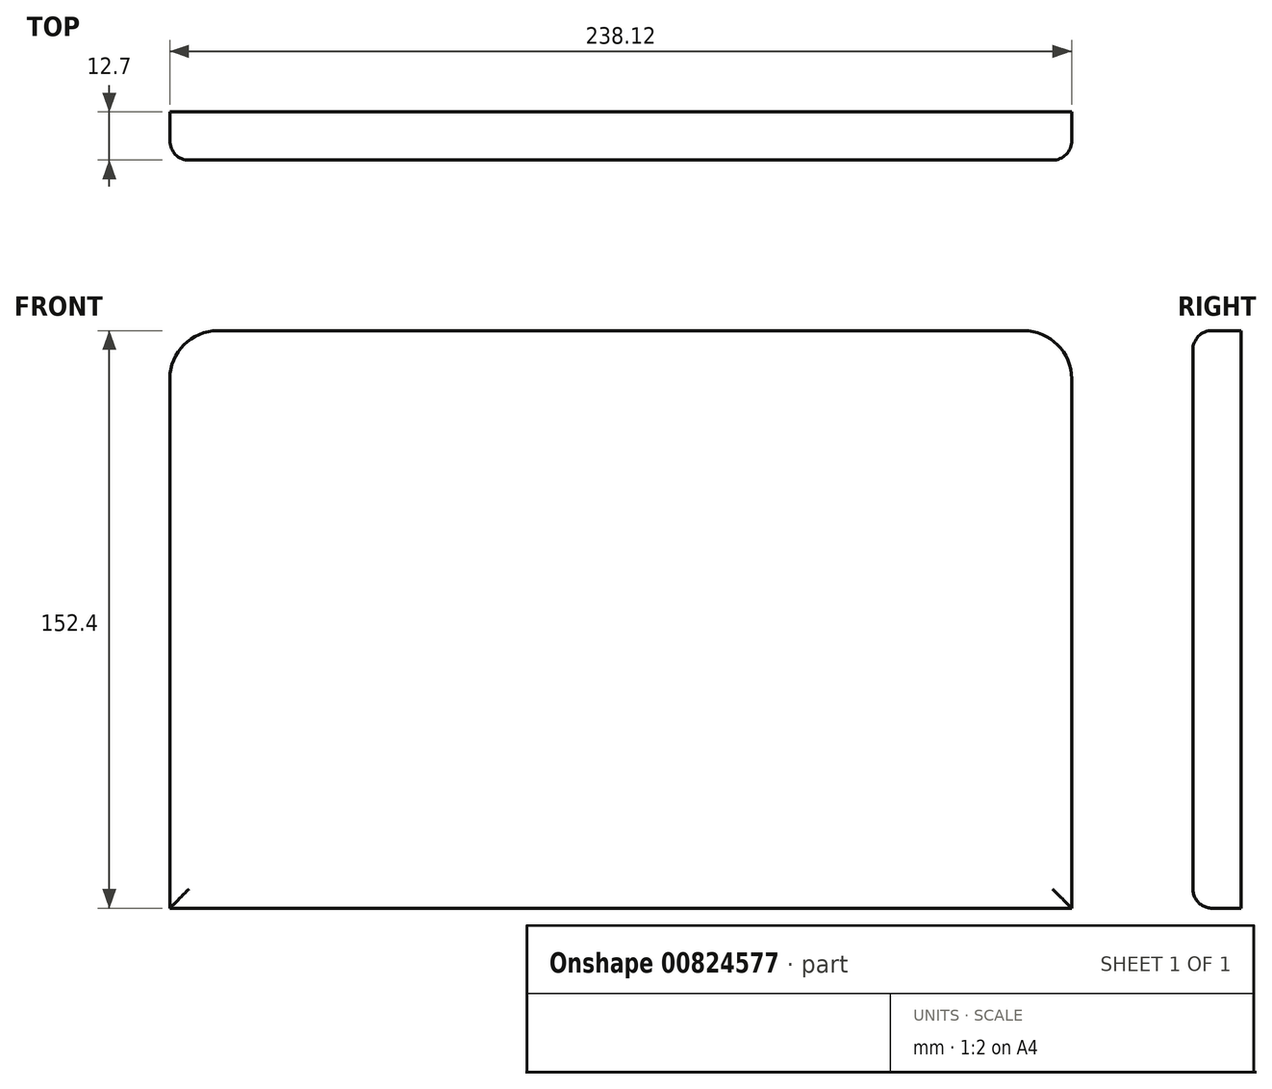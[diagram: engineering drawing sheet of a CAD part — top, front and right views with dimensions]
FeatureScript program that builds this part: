
annotation { "Feature Type Name" : "Feature", "Feature Type Description" : "" }
export const myFeature = defineFeature(function(context is Context, id is Id, definition is map)
    precondition{}
    {
        {
            var Q0;
            Q0=qCreatedBy(makeId("Front.planeOp"),FACE);
            var sketch = newSketch(context, id + "F0", { "sketchPlane" : qUnion([Q0])});
            skLineSegment(sketch, "E0.bottom", {"start": v(-119.06, -76.2) * mm, "end": v(119.06, -76.2) * mm});
            skLineSegment(sketch, "E0.top", {"start": v(-106.36, 76.2) * mm, "end": v(106.36, 76.2) * mm});
            skLineSegment(sketch, "E0.left", {"start": v(-119.06, -76.2) * mm, "end": v(-119.06, 63.5) * mm});
            skLineSegment(sketch, "E0.right", {"start": v(119.06, -76.2) * mm, "end": v(119.06, 63.5) * mm});
            skPoint(sketch, "E0.middle", {"position": v(0, 0) * mm});
            skPoint(sketch, "E1.visualSharp", {"position": v(-119.06, 76.2) * mm});
            skArc(sketch, "E1.filletArc", {"start": v(-106.36, 76.2) * mm, "mid": v(-115.34, 72.48) * mm, "end": v(-119.06, 63.5) * mm});
            skPoint(sketch, "E2.visualSharp", {"position": v(119.06, 76.2) * mm});
            skArc(sketch, "E2.filletArc", {"start": v(119.06, 63.5) * mm, "mid": v(115.34, 72.48) * mm, "end": v(106.36, 76.2) * mm});
            skSolve(sketch);
        }
        {
            var Q0;
            Q0=makeQuery(id+"F0.imprint","IMPRINT",FACE,{"disambiguationData":[TD([[makeQuery(id+"F0.imprint","IMPRINT",EDGE,{"derivedFrom":sQuery(id+"F0.wireOp",EDGE,"E0.bottom")}),1.0]])]});
            extrude(context, id + "F1", {"entities" : qUnion([Q0]), "depth" : 12.7 * mm, "offsetDistance" : 25.4 * mm});
        }
        {
            var Q0;
            Q0=makeQuery(id+"F1.opExtrude","CAP_FACE",FACE,{"disambiguationData":[OSD([sQuery(id+"F0.wireOp",EDGE,"E0.bottom"),sQuery(id+"F0.wireOp",EDGE,"E0.top"),sQuery(id+"F0.wireOp",EDGE,"E0.left"),sQuery(id+"F0.wireOp",EDGE,"E0.right"),sQuery(id+"F0.wireOp",EDGE,"E1.filletArc"),sQuery(id+"F0.wireOp",EDGE,"E2.filletArc")])],"isStart":false});
            fillet(context, id + "F2", {"entities" : qUnion([Q0]), "radius" : 5.08 * mm, "tangentPropagation" : true, "allowEdgeOverflow" : false});
        }
    });
